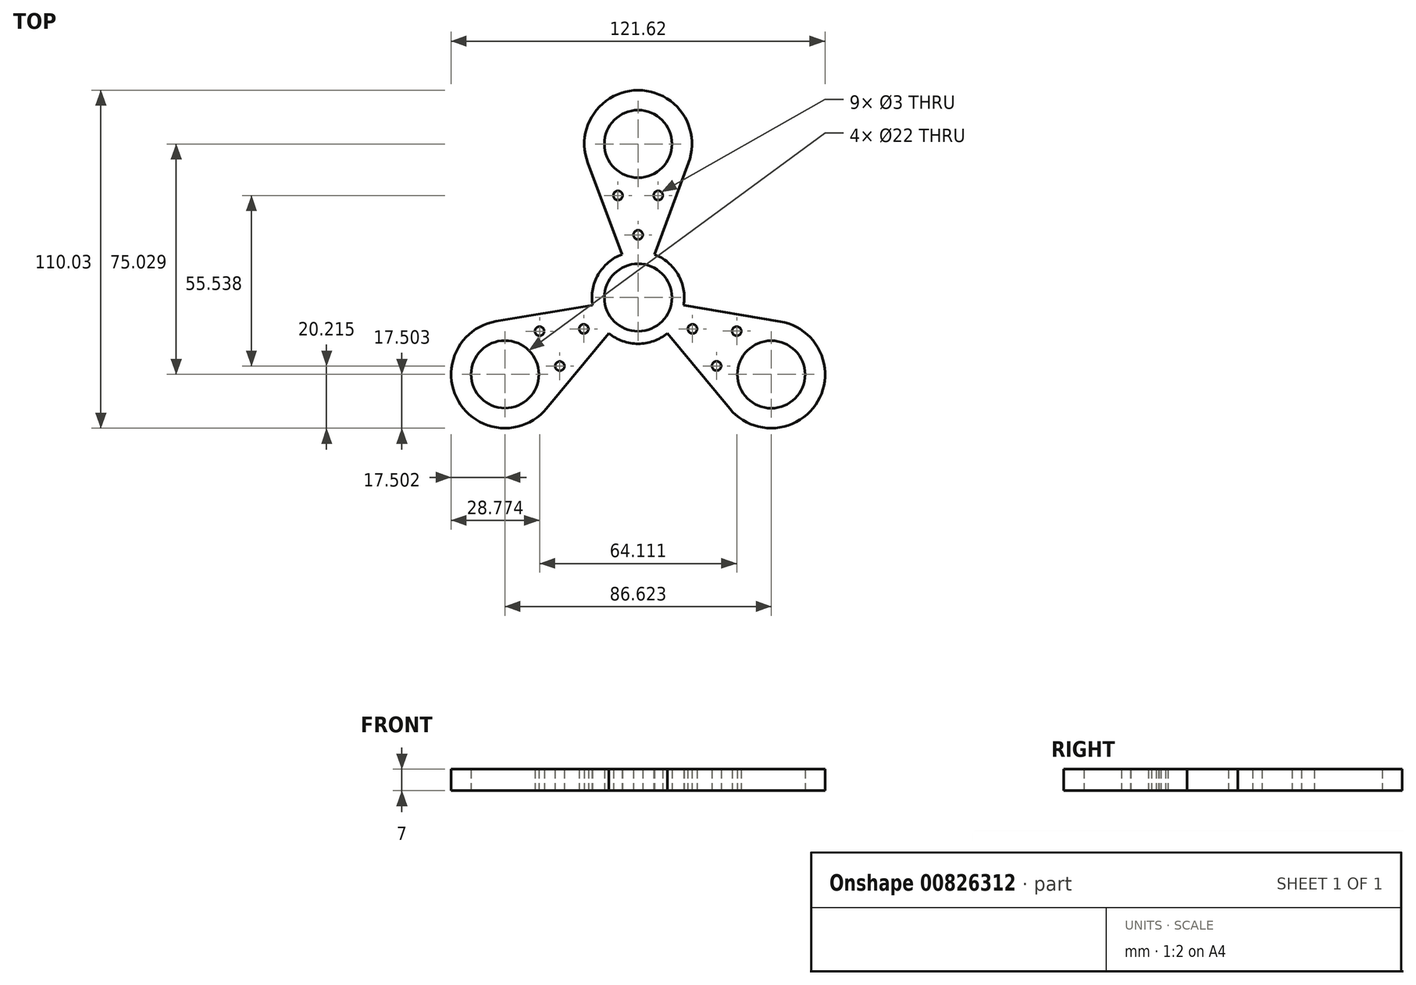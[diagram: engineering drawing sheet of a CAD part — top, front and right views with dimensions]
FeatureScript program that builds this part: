
annotation { "Feature Type Name" : "Feature", "Feature Type Description" : "" }
export const myFeature = defineFeature(function(context is Context, id is Id, definition is map)
    precondition{}
    {
        {
            var Q0;
            Q0=qCreatedBy(makeId("Top.planeOp"),FACE);
            var sketch = newSketch(context, id + "F0", { "sketchPlane" : qUnion([Q0])});
            skPoint(sketch, "E0.center", {"position": v(0, 0) * mm});
            skPoint(sketch, "E1.orphan", {"position": v(0.01, -11.02) * mm});
            skCircle(sketch, "E2.2.4", {"center": v(0.01, 50.01) * mm, "radius": 11 * mm});
            skPoint(sketch, "E2.2.10", {"position": v(0, -11) * mm});
            skCircle(sketch, "E2.2.23", {"center": v(0, 20.41) * mm, "radius": 1.5 * mm});
            skCircle(sketch, "E2.2.25", {"center": v(-6.57, 33.23) * mm, "radius": 1.5 * mm});
            skCircle(sketch, "E2.2.28", {"center": v(6.53, 33.23) * mm, "radius": 1.5 * mm});
            skArc(sketch, "E3", {"start": v(-5.24, 14.06) * mm, "mid": v(-9.68, 11.46) * mm, "end": v(-12.98, 7.51) * mm});
            skArc(sketch, "E4", {"start": v(16.4, 43.89) * mm, "mid": v(0.01, 67.51) * mm, "end": v(-16.38, 43.89) * mm});
            skLineSegment(sketch, "E5", {"start": v(-5.24, 14.06) * mm, "end": v(-16.38, 43.89) * mm});
            skLineSegment(sketch, "E6", {"start": v(5.26, 14.06) * mm, "end": v(16.4, 43.89) * mm});
            skArc(sketch, "E7.trimOffspring", {"start": v(13, 7.51) * mm, "mid": v(9.7, 11.46) * mm, "end": v(5.26, 14.06) * mm});
            skCircle(sketch, "E8.1.0", {"center": v(-43.32, -25) * mm, "radius": 11 * mm});
            skCircle(sketch, "E8.1.2", {"center": v(-17.68, -10.2) * mm, "radius": 1.5 * mm});
            skArc(sketch, "E8.1.3", {"start": v(-46.21, -7.73) * mm, "mid": v(-58.47, -33.74) * mm, "end": v(-29.82, -36.13) * mm});
            skArc(sketch, "E8.1.7", {"start": v(-12.98, 7.51) * mm, "mid": v(-14.76, 2.68) * mm, "end": v(-14.81, -2.47) * mm});
            skCircle(sketch, "E8.1.9", {"center": v(-32.05, -10.96) * mm, "radius": 1.5 * mm});
            skLineSegment(sketch, "E8.1.10", {"start": v(-9.56, -11.57) * mm, "end": v(-29.82, -36.13) * mm});
            skCircle(sketch, "E8.1.12", {"center": v(-25.5, -22.3) * mm, "radius": 1.5 * mm});
            skLineSegment(sketch, "E8.1.13", {"start": v(-14.81, -2.47) * mm, "end": v(-46.21, -7.73) * mm});
            skArc(sketch, "E8.1.14", {"start": v(-9.56, -11.57) * mm, "mid": v(-5.08, -14.13) * mm, "end": v(0, -15.02) * mm});
            skCircle(sketch, "E8.2.0", {"center": v(43.3, -25.02) * mm, "radius": 11 * mm});
            skCircle(sketch, "E8.2.2", {"center": v(17.68, -10.2) * mm, "radius": 1.5 * mm});
            skArc(sketch, "E8.2.3", {"start": v(29.8, -36.15) * mm, "mid": v(58.46, -33.77) * mm, "end": v(46.2, -7.76) * mm});
            skArc(sketch, "E8.2.7", {"start": v(0, -15.02) * mm, "mid": v(5.07, -14.13) * mm, "end": v(9.55, -11.59) * mm});
            skPoint(sketch, "E8.2.8", {"position": v(0, -11.04) * mm});
            skCircle(sketch, "E8.2.9", {"center": v(25.51, -22.27) * mm, "radius": 1.5 * mm});
            skLineSegment(sketch, "E8.2.10", {"start": v(14.8, -2.5) * mm, "end": v(46.2, -7.76) * mm});
            skCircle(sketch, "E8.2.12", {"center": v(32.06, -10.93) * mm, "radius": 1.5 * mm});
            skLineSegment(sketch, "E8.2.13", {"start": v(9.55, -11.59) * mm, "end": v(29.8, -36.15) * mm});
            skArc(sketch, "E8.2.14", {"start": v(14.8, -2.5) * mm, "mid": v(14.77, 2.66) * mm, "end": v(13, 7.51) * mm});
            skPoint(sketch, "E9.orphan", {"position": v(-0.02, 0) * mm});
            skCircle(sketch, "E10", {"center": v(0.01, 0.01) * mm, "radius": 11 * mm});
            skSolve(sketch);
        }
        {
            var Q0;
            Q0 = qSketchRegion(id + "F0", true);
            extrude(context, id + "F1", {"entities" : qUnion([Q0]), "depth" : 7 * mm, "offsetDistance" : 25 * mm});
        }
    });
